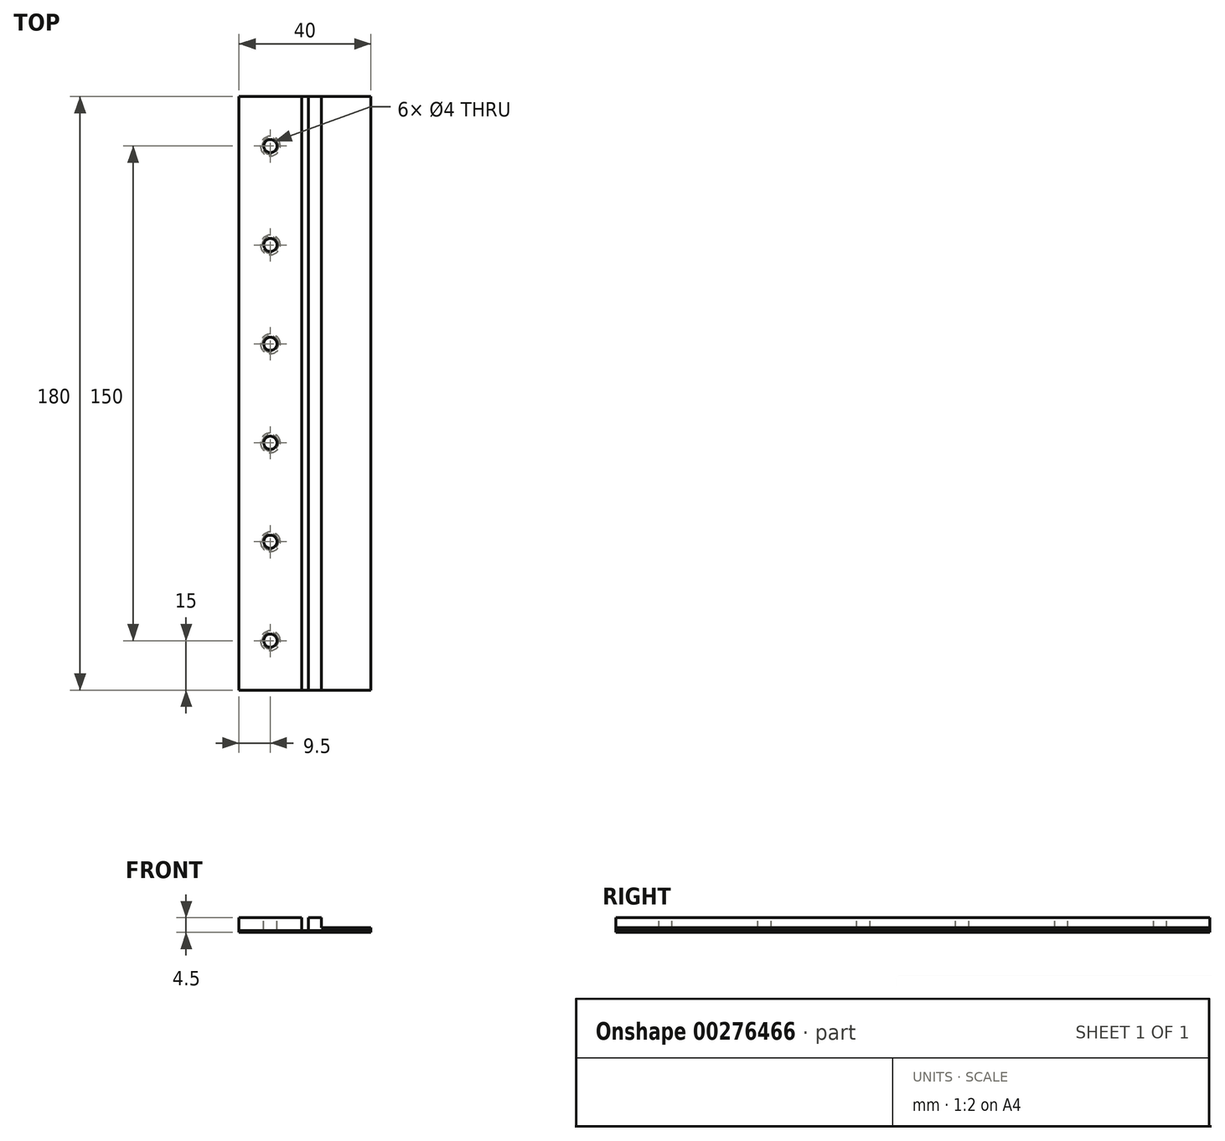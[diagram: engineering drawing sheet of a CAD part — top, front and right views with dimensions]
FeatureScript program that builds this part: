
annotation { "Feature Type Name" : "Feature", "Feature Type Description" : "" }
export const myFeature = defineFeature(function(context is Context, id is Id, definition is map)
    precondition{}
    {
        {
            var Q0;
            Q0=qCreatedBy(makeId("Top.planeOp"),FACE);
            var sketch = newSketch(context, id + "F0", { "sketchPlane" : qUnion([Q0])});
            skLineSegment(sketch, "E0.bottom", {"start": v(20, -90) * mm, "end": v(-20, -90) * mm});
            skLineSegment(sketch, "E0.top", {"start": v(20, 90) * mm, "end": v(-20, 90) * mm});
            skLineSegment(sketch, "E0.left", {"start": v(20, -90) * mm, "end": v(20, 90) * mm});
            skLineSegment(sketch, "E0.right", {"start": v(-20, -90) * mm, "end": v(-20, 90) * mm});
            skPoint(sketch, "E0.middle", {"position": v(0, 0) * mm});
            skSolve(sketch);
        }
        {
            var Q0;
            Q0 = qSketchRegion(id + "F0", true);
            extrude(context, id + "F1", {"entities" : qUnion([Q0]), "depth" : .5 * mm});
        }
        {
            var Q0;
            Q0=makeQuery(id+"F1.opExtrude","CAP_FACE",FACE,{"disambiguationData":[OSD([sQuery(id+"F0.wireOp",EDGE,"E0.bottom"),sQuery(id+"F0.wireOp",EDGE,"E0.top"),sQuery(id+"F0.wireOp",EDGE,"E0.left"),sQuery(id+"F0.wireOp",EDGE,"E0.right")])],"isStart":false});
            var sketch = newSketch(context, id + "F2", { "sketchPlane" : qUnion([Q0])});
            skLineSegment(sketch, "E1.bottom", {"start": v(20, 90) * mm, "end": v(1, 90) * mm});
            skLineSegment(sketch, "E1.top", {"start": v(20, -90) * mm, "end": v(1, -90) * mm});
            skLineSegment(sketch, "E1.left", {"start": v(20, 90) * mm, "end": v(20, -90) * mm});
            skLineSegment(sketch, "E1.right", {"start": v(1, 90) * mm, "end": v(1, -90) * mm});
            skLineSegment(sketch, "E2.bottom", {"start": v(-20, 90) * mm, "end": v(-1, 90) * mm});
            skLineSegment(sketch, "E2.top", {"start": v(-20, -90) * mm, "end": v(-1, -90) * mm});
            skLineSegment(sketch, "E2.left", {"start": v(-20, 90) * mm, "end": v(-20, -90) * mm});
            skLineSegment(sketch, "E2.right", {"start": v(-1, 90) * mm, "end": v(-1, -90) * mm});
            skSolve(sketch);
        }
        {
            var Q0;
            Q0 = qSketchRegion(id + "F2", true);
            extrude(context, id + "F3", {"entities" : qUnion([Q0]), "depth" : 4 * mm});
        }
        {
            var Q0;
            Q0=makeQuery(id+"F3.opExtrude","CAP_FACE",FACE,{"disambiguationData":[OSD([sQuery(id+"F2.wireOp",EDGE,"E1.bottom"),sQuery(id+"F2.wireOp",EDGE,"E1.top"),sQuery(id+"F2.wireOp",EDGE,"E1.left"),sQuery(id+"F2.wireOp",EDGE,"E1.right")])],"isStart":false});
            var sketch = newSketch(context, id + "F4", { "sketchPlane" : qUnion([Q0])});
            skLineSegment(sketch, "E3.bottom", {"start": v(5, 90) * mm, "end": v(20, 90) * mm});
            skLineSegment(sketch, "E3.top", {"start": v(5, -90) * mm, "end": v(20, -90) * mm});
            skLineSegment(sketch, "E3.left", {"start": v(5, 90) * mm, "end": v(5, -90) * mm});
            skLineSegment(sketch, "E3.right", {"start": v(20, 90) * mm, "end": v(20, -90) * mm});
            skSolve(sketch);
        }
        {
            var Q0;
            Q0 = qSketchRegion(id + "F4", true);
            extrude(context, id + "F5", {"entities" : qUnion([Q0]), "operationType" : NewBodyOperationType.REMOVE, "oppositeDirection" : true, "depth" : 3 * mm});
        }
        {
            var Q0;
            Q0=makeQuery(id+"F3.opExtrude","CAP_FACE",FACE,{"disambiguationData":[OSD([sQuery(id+"F2.wireOp",EDGE,"E2.bottom"),sQuery(id+"F2.wireOp",EDGE,"E2.top"),sQuery(id+"F2.wireOp",EDGE,"E2.left"),sQuery(id+"F2.wireOp",EDGE,"E2.right")])],"isStart":false});
            var sketch = newSketch(context, id + "F6", { "sketchPlane" : qUnion([Q0])});
            skCircle(sketch, "E4", {"center": v(-10.5, 15) * mm, "radius": 2 * mm});
            skCircle(sketch, "E5", {"center": v(-10.5, 45) * mm, "radius": 2 * mm});
            skCircle(sketch, "E6", {"center": v(-10.5, 75) * mm, "radius": 2 * mm});
            skLineSegment(sketch, "E7", {"start": v(-10.5, 0) * mm, "end": v(-10.5, 90) * mm, "construction": true});
            skCircle(sketch, "E8.MirrorC", {"center": v(-10.5, -45) * mm, "radius": 2 * mm});
            skCircle(sketch, "E9.MirrorC", {"center": v(-10.5, -15) * mm, "radius": 2 * mm});
            skCircle(sketch, "E10.MirrorC", {"center": v(-10.5, -75) * mm, "radius": 2 * mm});
            skSolve(sketch);
        }
        {
            var Q0;
            Q0 = qSketchRegion(id + "F6", true);
            extrude(context, id + "F7", {"entities" : qUnion([Q0]), "operationType" : NewBodyOperationType.REMOVE, "endBound" : BoundingType.THROUGH_ALL, "oppositeDirection" : true, "depth" : 25 * mm});
        }
        {
            var Q0;
            Q0=makeQuery(id+"F7.boolean.opBoolean","INTERSECT",EDGE,{"derivedFrom":[makeQuery(id+"F1.opExtrude","CAP_FACE",FACE,{"disambiguationData":[OSD([sQuery(id+"F0.wireOp",EDGE,"E0.bottom"),sQuery(id+"F0.wireOp",EDGE,"E0.top"),sQuery(id+"F0.wireOp",EDGE,"E0.left"),sQuery(id+"F0.wireOp",EDGE,"E0.right")])],"isStart":true}),makeQuery(id+"F7.opExtrude","SWEPT_FACE",FACE,{"disambiguationData":[OSD([sQuery(id+"F6.wireOp",EDGE,"E10.MirrorC")])]})]});
            var Q1;
            Q1=makeQuery(id+"F7.boolean.opBoolean","INTERSECT",EDGE,{"derivedFrom":[makeQuery(id+"F1.opExtrude","CAP_FACE",FACE,{"disambiguationData":[OSD([sQuery(id+"F0.wireOp",EDGE,"E0.bottom"),sQuery(id+"F0.wireOp",EDGE,"E0.top"),sQuery(id+"F0.wireOp",EDGE,"E0.left"),sQuery(id+"F0.wireOp",EDGE,"E0.right")])],"isStart":true}),makeQuery(id+"F7.opExtrude","SWEPT_FACE",FACE,{"disambiguationData":[OSD([sQuery(id+"F6.wireOp",EDGE,"E8.MirrorC")])]})]});
            var Q2;
            Q2=makeQuery(id+"F7.boolean.opBoolean","INTERSECT",EDGE,{"derivedFrom":[makeQuery(id+"F1.opExtrude","CAP_FACE",FACE,{"disambiguationData":[OSD([sQuery(id+"F0.wireOp",EDGE,"E0.bottom"),sQuery(id+"F0.wireOp",EDGE,"E0.top"),sQuery(id+"F0.wireOp",EDGE,"E0.left"),sQuery(id+"F0.wireOp",EDGE,"E0.right")])],"isStart":true}),makeQuery(id+"F7.opExtrude","SWEPT_FACE",FACE,{"disambiguationData":[OSD([sQuery(id+"F6.wireOp",EDGE,"E9.MirrorC")])]})]});
            var Q3;
            Q3=makeQuery(id+"F7.boolean.opBoolean","INTERSECT",EDGE,{"derivedFrom":[makeQuery(id+"F1.opExtrude","CAP_FACE",FACE,{"disambiguationData":[OSD([sQuery(id+"F0.wireOp",EDGE,"E0.bottom"),sQuery(id+"F0.wireOp",EDGE,"E0.top"),sQuery(id+"F0.wireOp",EDGE,"E0.left"),sQuery(id+"F0.wireOp",EDGE,"E0.right")])],"isStart":true}),makeQuery(id+"F7.opExtrude","SWEPT_FACE",FACE,{"disambiguationData":[OSD([sQuery(id+"F6.wireOp",EDGE,"E4")])]})]});
            var Q4;
            Q4=makeQuery(id+"F7.boolean.opBoolean","INTERSECT",EDGE,{"derivedFrom":[makeQuery(id+"F1.opExtrude","CAP_FACE",FACE,{"disambiguationData":[OSD([sQuery(id+"F0.wireOp",EDGE,"E0.bottom"),sQuery(id+"F0.wireOp",EDGE,"E0.top"),sQuery(id+"F0.wireOp",EDGE,"E0.left"),sQuery(id+"F0.wireOp",EDGE,"E0.right")])],"isStart":true}),makeQuery(id+"F7.opExtrude","SWEPT_FACE",FACE,{"disambiguationData":[OSD([sQuery(id+"F6.wireOp",EDGE,"E5")])]})]});
            var Q5;
            Q5=makeQuery(id+"F7.boolean.opBoolean","INTERSECT",EDGE,{"derivedFrom":[makeQuery(id+"F1.opExtrude","CAP_FACE",FACE,{"disambiguationData":[OSD([sQuery(id+"F0.wireOp",EDGE,"E0.bottom"),sQuery(id+"F0.wireOp",EDGE,"E0.top"),sQuery(id+"F0.wireOp",EDGE,"E0.left"),sQuery(id+"F0.wireOp",EDGE,"E0.right")])],"isStart":true}),makeQuery(id+"F7.opExtrude","SWEPT_FACE",FACE,{"disambiguationData":[OSD([sQuery(id+"F6.wireOp",EDGE,"E6")])]})]});
            chamfer(context, id + "F8", {"entities" : qUnion([Q0, Q1, Q2, Q3, Q4, Q5]), "width" : 1 * mm, "tangentPropagation" : true});
        }
    });
